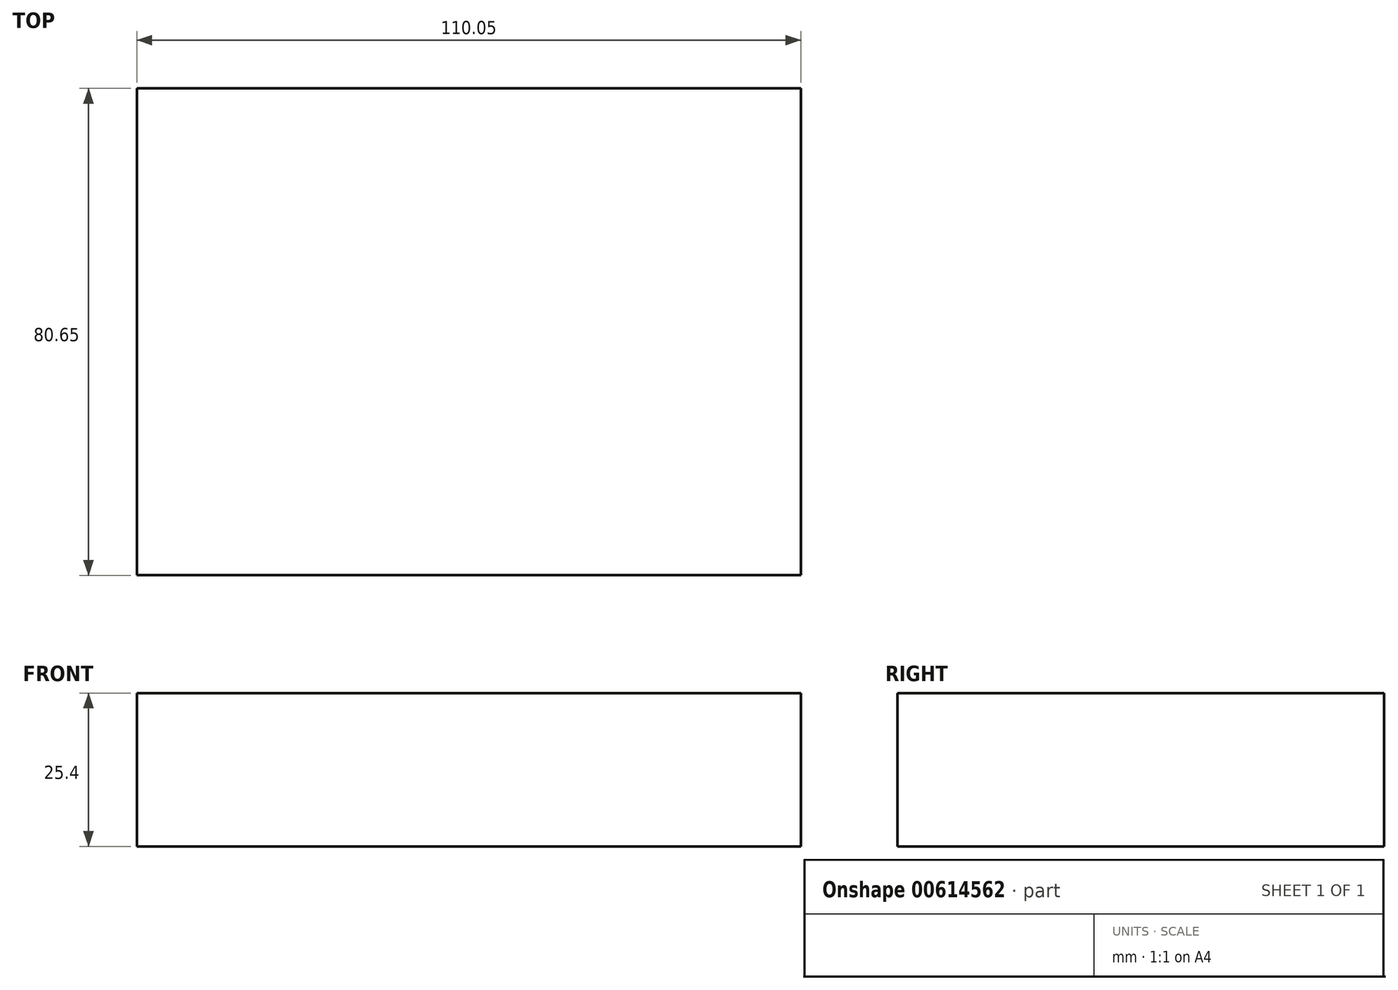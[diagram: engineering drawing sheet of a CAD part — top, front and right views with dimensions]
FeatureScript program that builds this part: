
annotation { "Feature Type Name" : "Feature", "Feature Type Description" : "" }
export const myFeature = defineFeature(function(context is Context, id is Id, definition is map)
    precondition{}
    {
        {
            var Q0;
            Q0=qCreatedBy(makeId("Top.planeOp"),FACE);
            var sketch = newSketch(context, id + "F0", { "sketchPlane" : qUnion([Q0])});
            skLineSegment(sketch, "E0.bottom", {"start": v(-100.2, 41.68) * mm, "end": v(9.85, 41.68) * mm});
            skLineSegment(sketch, "E0.top", {"start": v(-100.2, -38.97) * mm, "end": v(9.85, -38.97) * mm});
            skLineSegment(sketch, "E0.left", {"start": v(-100.2, 41.68) * mm, "end": v(-100.2, -38.97) * mm});
            skLineSegment(sketch, "E0.right", {"start": v(9.85, 41.68) * mm, "end": v(9.85, -38.97) * mm});
            skSolve(sketch);
        }
        {
            var Q0;
            Q0=makeQuery(id+"F0.imprint","IMPRINT",FACE,{"disambiguationData":[TD([[makeQuery(id+"F0.imprint","IMPRINT",EDGE,{"derivedFrom":sQuery(id+"F0.wireOp",EDGE,"E0.bottom")}),-1.0]])]});
            extrude(context, id + "F1", {"entities" : qUnion([Q0]), "depth" : 25.4 * mm, "offsetDistance" : 25.4 * mm});
        }
    });
